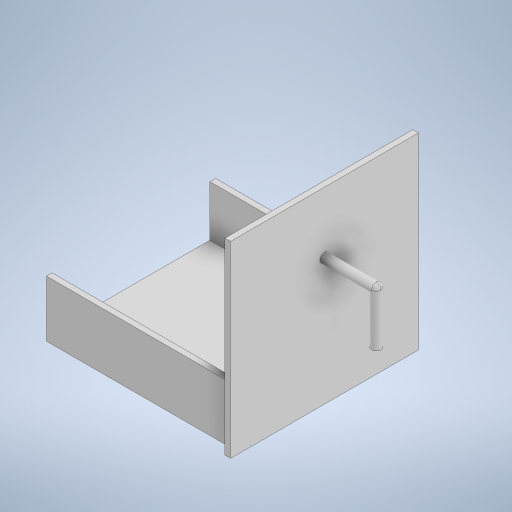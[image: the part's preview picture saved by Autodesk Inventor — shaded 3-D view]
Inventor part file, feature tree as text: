
AUTODESK INVENTOR PART (.ipt)
format: ipt  version: 2024.3 (Build 283343000, 343)  size: 260,608 bytes
history: native  units: mm
features: extrude x3, sketch x3, fillet x1
ambient origin geometry x8: Origin, YZ Plane, XZ Plane, XY Plane, X Axis, Y Axis, Z Axis, Center Point
bodies: Solid1 (feature_tree)
feature tree (7):
  extrude  "Extrusion1"  Depth=90.0mm
  extrude  "Extrusion2"  TaperAngle=0.0deg  [1 undecoded]
  extrude  "Extrusion3"  Depth=3.0mm
  fillet  "Fillet1"  Radius=3.0mm
  sketch  "Sketch1"  dims[d0=45.0mm d1=90.0mm]
  sketch  "Sketch2"  dims[d2=30.0mm d3=0.0mm]
  sketch  "Sketch4"  dims[d4=3.0mm d5=3.0mm d6=3.0mm d7=100.0mm d8=0.0mm d9=100.0mm d10=100.0mm d11=3.0mm d12=0.0mm d13=5.0mm d14=5.0mm d15=30.0mm d16=30.0mm d17=30.0mm d18=5.0mm d19=0.0mm d20=2.5mm]
note: 1 required parameter value undecoded (feature->parameter linkage not recoverable at this tier; creation-order binding heuristic only, values carry confidence <= 0.55)
